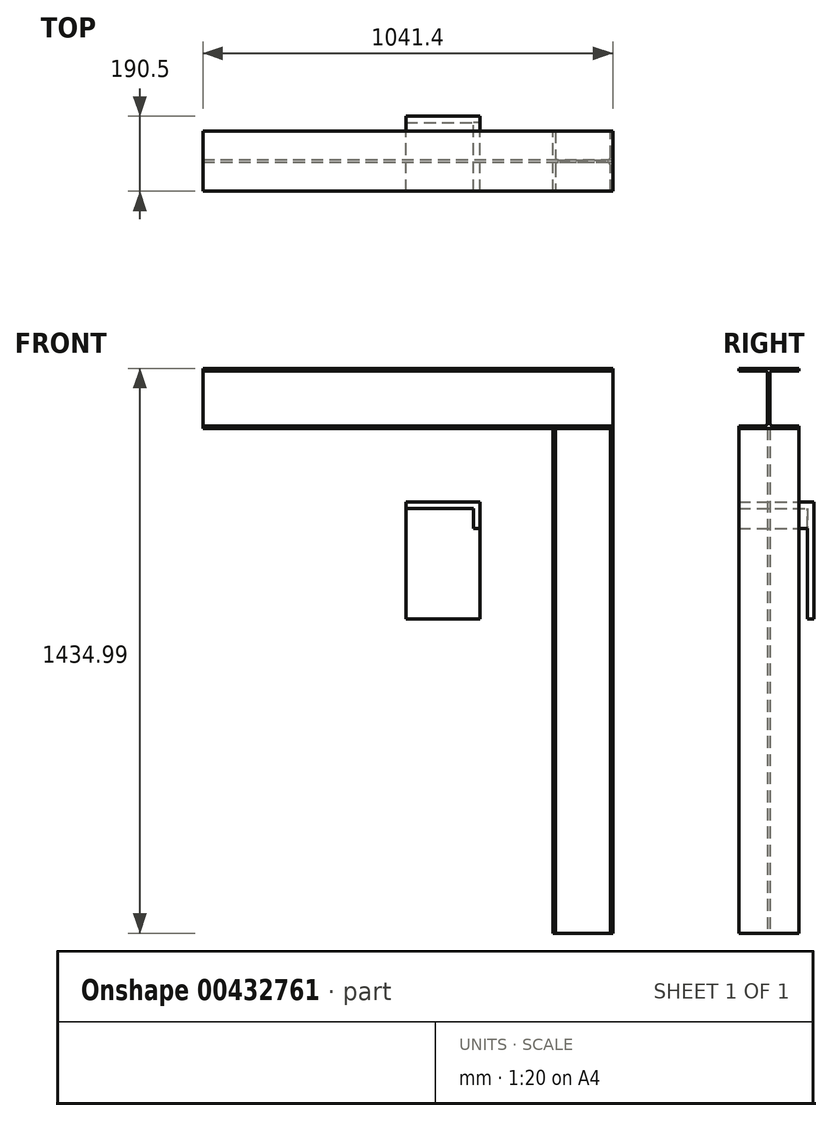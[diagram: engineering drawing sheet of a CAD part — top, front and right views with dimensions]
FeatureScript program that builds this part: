
annotation { "Feature Type Name" : "Feature", "Feature Type Description" : "" }
export const myFeature = defineFeature(function(context is Context, id is Id, definition is map)
    precondition{}
    {
        {
            var Q0;
            Q0=qCreatedBy(makeId("Right.planeOp"),FACE);
            var sketch = newSketch(context, id + "F0", { "sketchPlane" : qUnion([Q0])});
            skPoint(sketch, "E0", {"position": v(0, 279.4) * mm});
            skLineSegment(sketch, "E1", {"start": v(-76.2, 355.49) * mm, "end": v(76.2, 355.49) * mm});
            skLineSegment(sketch, "E2", {"start": v(76.2, 355.49) * mm, "end": v(76.2, 349.14) * mm});
            skLineSegment(sketch, "E3", {"start": v(76.2, 349.14) * mm, "end": v(10.17, 349.14) * mm});
            skLineSegment(sketch, "E4", {"start": v(3.17, 342.14) * mm, "end": v(3.17, 216.44) * mm});
            skLineSegment(sketch, "E5", {"start": v(10.17, 209.44) * mm, "end": v(76.2, 209.44) * mm});
            skLineSegment(sketch, "E6", {"start": v(76.2, 209.44) * mm, "end": v(76.2, 203.09) * mm});
            skLineSegment(sketch, "E7", {"start": v(76.2, 203.09) * mm, "end": v(-76.2, 203.09) * mm});
            skLineSegment(sketch, "E8", {"start": v(-76.2, 203.09) * mm, "end": v(-76.2, 209.44) * mm});
            skLineSegment(sketch, "E9", {"start": v(-76.2, 209.44) * mm, "end": v(-10.18, 209.44) * mm});
            skLineSegment(sketch, "E10", {"start": v(-3.18, 216.44) * mm, "end": v(-3.18, 342.14) * mm});
            skLineSegment(sketch, "E11", {"start": v(-10.18, 349.14) * mm, "end": v(-76.2, 349.14) * mm});
            skLineSegment(sketch, "E12", {"start": v(-76.2, 349.14) * mm, "end": v(-76.2, 355.49) * mm});
            skPoint(sketch, "E13.visualSharp", {"position": v(3.17, 349.14) * mm});
            skArc(sketch, "E13.filletArc", {"start": v(10.17, 349.14) * mm, "mid": v(5.22, 347.09) * mm, "end": v(3.17, 342.14) * mm});
            skPoint(sketch, "E14.visualSharp", {"position": v(-3.18, 349.14) * mm});
            skArc(sketch, "E14.filletArc", {"start": v(-3.18, 342.14) * mm, "mid": v(-5.23, 347.09) * mm, "end": v(-10.18, 349.14) * mm});
            skPoint(sketch, "E15.visualSharp", {"position": v(3.17, 209.44) * mm});
            skArc(sketch, "E15.filletArc", {"start": v(3.17, 216.44) * mm, "mid": v(5.22, 211.49) * mm, "end": v(10.17, 209.44) * mm});
            skPoint(sketch, "E16.visualSharp", {"position": v(-3.18, 209.44) * mm});
            skArc(sketch, "E16.filletArc", {"start": v(-10.18, 209.44) * mm, "mid": v(-5.23, 211.49) * mm, "end": v(-3.18, 216.44) * mm});
            skPoint(sketch, "E17", {"position": v(0, 355.49) * mm});
            skPoint(sketch, "E18", {"position": v(0, 203.09) * mm});
            skLineSegment(sketch, "E19", {"start": v(0, 355.49) * mm, "end": v(0, 203.09) * mm, "construction": true});
            skLineSegment(sketch, "E20", {"start": v(0, 279.29) * mm, "end": v(3.17, 279.29) * mm, "construction": true});
            skLineSegment(sketch, "E21", {"start": v(3.17, 279.29) * mm, "end": v(0, 279.29) * mm, "construction": true});
            skLineSegment(sketch, "E22", {"start": v(-3.18, 279.29) * mm, "end": v(0, 279.29) * mm, "construction": true});
            skPoint(sketch, "E23", {"position": v(0, 279.29) * mm});
            skSolve(sketch);
        }
        {
            var Q0;
            Q0 = qSketchRegion(id + "F0", true);
            extrude(context, id + "F1", {"entities" : qUnion([Q0]), "depth" : 431.8 * mm, "hasSecondDirection" : true, "secondDirectionOppositeDirection" : true, "secondDirectionDepth" : 609.6 * mm});
        }
        {
            var Q0;
            Q0=qCreatedBy(makeId("Top.planeOp"),FACE);
            var sketch = newSketch(context, id + "F2", { "sketchPlane" : qUnion([Q0])});
            skPoint(sketch, "E24", {"position": v(435.74, -360.93) * mm});
            skLineSegment(sketch, "E25", {"start": v(431.8, 76.2) * mm, "end": v(431.8, -76.2) * mm});
            skLineSegment(sketch, "E26", {"start": v(431.8, -76.2) * mm, "end": v(425.45, -76.2) * mm});
            skLineSegment(sketch, "E27", {"start": v(425.45, -76.2) * mm, "end": v(425.45, -10.18) * mm});
            skLineSegment(sketch, "E28", {"start": v(418.45, -3.18) * mm, "end": v(292.75, -3.18) * mm});
            skLineSegment(sketch, "E29", {"start": v(285.75, -10.18) * mm, "end": v(285.75, -76.2) * mm});
            skLineSegment(sketch, "E30", {"start": v(285.75, -76.2) * mm, "end": v(279.4, -76.2) * mm});
            skLineSegment(sketch, "E31", {"start": v(279.4, -76.2) * mm, "end": v(279.4, 76.2) * mm});
            skLineSegment(sketch, "E32", {"start": v(279.4, 76.2) * mm, "end": v(285.75, 76.2) * mm});
            skLineSegment(sketch, "E33", {"start": v(285.75, 76.2) * mm, "end": v(285.75, 10.17) * mm});
            skLineSegment(sketch, "E34", {"start": v(292.75, 3.17) * mm, "end": v(418.45, 3.17) * mm});
            skLineSegment(sketch, "E35", {"start": v(425.45, 10.17) * mm, "end": v(425.45, 76.2) * mm});
            skLineSegment(sketch, "E36", {"start": v(425.45, 76.2) * mm, "end": v(431.8, 76.2) * mm});
            skPoint(sketch, "E37.visualSharp", {"position": v(425.45, -3.18) * mm});
            skArc(sketch, "E37.filletArc", {"start": v(425.45, -10.18) * mm, "mid": v(423.4, -5.23) * mm, "end": v(418.45, -3.18) * mm});
            skPoint(sketch, "E38.visualSharp", {"position": v(425.45, 3.17) * mm});
            skArc(sketch, "E38.filletArc", {"start": v(418.45, 3.17) * mm, "mid": v(423.4, 5.22) * mm, "end": v(425.45, 10.17) * mm});
            skPoint(sketch, "E39.visualSharp", {"position": v(285.75, -3.18) * mm});
            skArc(sketch, "E39.filletArc", {"start": v(292.75, -3.18) * mm, "mid": v(287.8, -5.23) * mm, "end": v(285.75, -10.18) * mm});
            skPoint(sketch, "E40.visualSharp", {"position": v(285.75, 3.17) * mm});
            skArc(sketch, "E40.filletArc", {"start": v(285.75, 10.17) * mm, "mid": v(287.8, 5.22) * mm, "end": v(292.75, 3.17) * mm});
            skPoint(sketch, "E41", {"position": v(431.8, 0) * mm});
            skPoint(sketch, "E42", {"position": v(279.4, 0) * mm});
            skLineSegment(sketch, "E43", {"start": v(431.8, 0) * mm, "end": v(279.4, 0) * mm, "construction": true});
            skLineSegment(sketch, "E44", {"start": v(355.6, 0) * mm, "end": v(355.6, -3.18) * mm, "construction": true});
            skLineSegment(sketch, "E45", {"start": v(355.6, -3.18) * mm, "end": v(355.6, 0) * mm, "construction": true});
            skLineSegment(sketch, "E46", {"start": v(355.6, 3.17) * mm, "end": v(355.6, 0) * mm, "construction": true});
            skPoint(sketch, "E47", {"position": v(355.6, 0) * mm});
            skSolve(sketch);
        }
        {
            var Q0;
            Q0=makeQuery(id+"F2.imprint","IMPRINT",FACE,{"disambiguationData":[TD([[makeQuery(id+"F2.imprint","IMPRINT",EDGE,{"derivedFrom":sQuery(id+"F2.wireOp",EDGE,"E25")}),-1.0]])]});
            extrude(context, id + "F3", {"entities" : qUnion([Q0]), "depth" : 203.2 * mm, "hasSecondDirection" : true, "secondDirectionOppositeDirection" : true, "secondDirectionDepth" : 1079.5 * mm});
        }
        {
            var Q0;
            Q0=qCreatedBy(makeId("Front.planeOp"),FACE);
            var sketch = newSketch(context, id + "F4", { "sketchPlane" : qUnion([Q0])});
            skLineSegment(sketch, "E48.bottom", {"start": v(-93.98, 15.87) * mm, "end": v(93.98, 15.87) * mm});
            skLineSegment(sketch, "E48.top", {"start": v(-93.98, 0) * mm, "end": v(93.98, 0) * mm});
            skLineSegment(sketch, "E48.left", {"start": v(93.98, 15.87) * mm, "end": v(93.98, 0) * mm});
            skLineSegment(sketch, "E48.right", {"start": v(-93.98, 15.87) * mm, "end": v(-93.98, 0) * mm});
            skSolve(sketch);
        }
        {
            var Q0;
            Q0 = qSketchRegion(id + "F4", true);
            extrude(context, id + "F5", {"entities" : qUnion([Q0]), "depth" : 76.2 * mm, "hasSecondDirection" : true, "secondDirectionOppositeDirection" : true, "secondDirectionDepth" : 114.3 * mm});
        }
        {
            var Q0;
            Q0=qCreatedBy(makeId("Top.planeOp"),FACE);
            var sketch = newSketch(context, id + "F6", { "sketchPlane" : qUnion([Q0])});
            skLineSegment(sketch, "E49.bottom", {"start": v(-93.98, 98.42) * mm, "end": v(93.98, 98.42) * mm});
            skLineSegment(sketch, "E49.top", {"start": v(-93.98, 114.3) * mm, "end": v(93.98, 114.3) * mm});
            skLineSegment(sketch, "E49.left", {"start": v(-93.98, 98.42) * mm, "end": v(-93.98, 114.3) * mm});
            skLineSegment(sketch, "E49.right", {"start": v(93.98, 98.42) * mm, "end": v(93.98, 114.3) * mm});
            skSolve(sketch);
        }
        {
            var Q0;
            Q0 = qSketchRegion(id + "F6", true);
            extrude(context, id + "F7", {"entities" : qUnion([Q0]), "operationType" : NewBodyOperationType.ADD, "oppositeDirection" : true, "depth" : 281.3 * mm});
        }
        {
            var Q0;
            Q0=qCreatedBy(makeId("Front.planeOp"),FACE);
            var sketch = newSketch(context, id + "F8", { "sketchPlane" : qUnion([Q0])});
            skLineSegment(sketch, "E50.MirrorCS", {"start": v(93.98, -50.8) * mm, "end": v(78.1, -50.8) * mm});
            skLineSegment(sketch, "E51.MirrorCS", {"start": v(78.1, 0) * mm, "end": v(78.1, -50.8) * mm});
            skLineSegment(sketch, "E52.MirrorCS", {"start": v(93.98, 0) * mm, "end": v(78.1, 0) * mm});
            skLineSegment(sketch, "E53", {"start": v(93.98, 0) * mm, "end": v(93.98, -50.8) * mm});
            skSolve(sketch);
        }
        {
            var Q0;
            Q0 = qSketchRegion(id + "F8", true);
            var Q1;
            Q1=makeQuery(id+"F5.opExtrude","CAP_FACE",FACE,{"disambiguationData":[OSD([sQuery(id+"F4.wireOp",EDGE,"E48.bottom"),sQuery(id+"F4.wireOp",EDGE,"E48.top"),sQuery(id+"F4.wireOp",EDGE,"E48.left"),sQuery(id+"F4.wireOp",EDGE,"E48.right")])],"isStart":false});
            extrude(context, id + "F9", {"entities" : qUnion([Q0]), "operationType" : NewBodyOperationType.ADD, "endBound" : BoundingType.UP_TO_SURFACE, "endBoundEntityFace" : qUnion([Q1]), "depth" : 68.07 * mm, "hasSecondDirection" : true, "secondDirectionBound" : SecondDirectionBoundingType.UP_TO_NEXT, "secondDirectionOppositeDirection" : true, "secondDirectionDepth" : 25.4 * mm});
        }
    });
